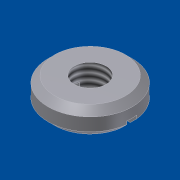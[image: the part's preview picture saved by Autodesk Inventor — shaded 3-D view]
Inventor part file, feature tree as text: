
AUTODESK INVENTOR PART (.ipt)
format: ipt  version: unknown  size: 185,856 bytes
history: native  units: mm
features: sketch x3, extrude x2, chamfer x1, hole x1
ambient origin geometry x8: Origin, YZ Plane, XZ Plane, XY Plane, X Axis, Y Axis, Z Axis, Center Point
feature tree (7):
  extrude  "Extrusion1"  Depth=4.0mm TaperAngle=0.0deg
  chamfer  "Chamfer1"  Distance=1.0mm Angle=45.0deg
  hole  "Hole1"  [1 undecoded]
  extrude  "Extrusion2"  [1 undecoded]
  sketch  "Sketch1"  dims[d0=13.0mm d1=4.0mm d2=0.0mm d3=1.0mm d4=2.0mm d5=45.0deg]
  sketch  "Sketch2"  dims[d6=4.917mm d7=6.0mm d8=4.0mm d9=2.0mm d10=90.0deg d11=8.0mm d12=20.594885mm d13=1.5mm]
  sketch  "Sketch3"  dims[d14=1.5mm d15=0.0mm]
note: 2 required parameter values undecoded (feature->parameter linkage not recoverable at this tier; creation-order binding heuristic only, values carry confidence <= 0.55)
